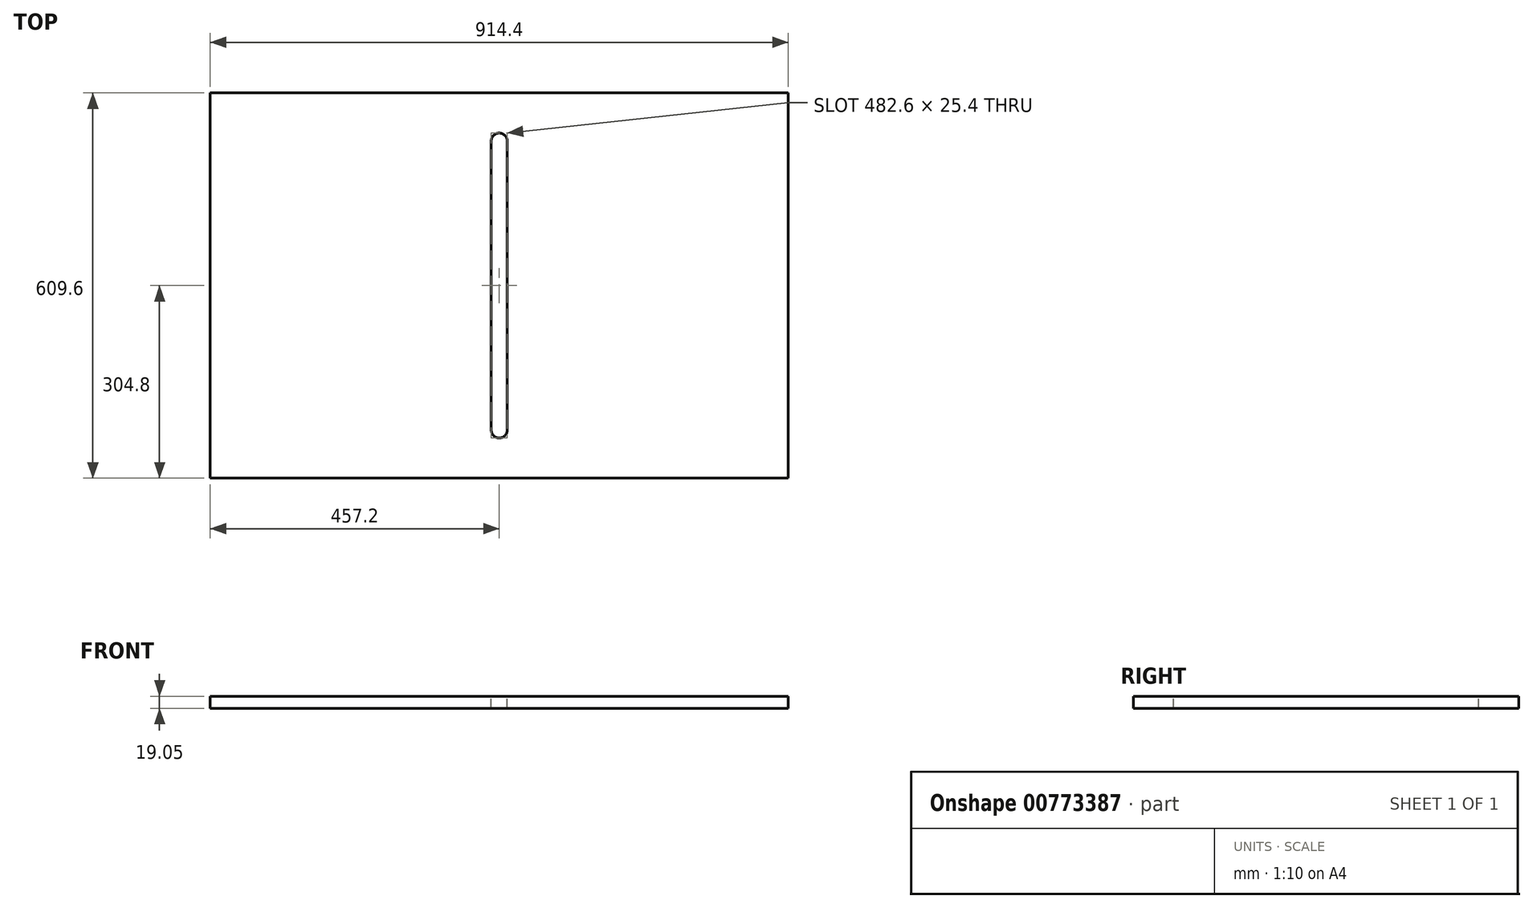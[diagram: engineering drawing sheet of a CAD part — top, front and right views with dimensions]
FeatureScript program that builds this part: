
annotation { "Feature Type Name" : "Feature", "Feature Type Description" : "" }
export const myFeature = defineFeature(function(context is Context, id is Id, definition is map)
    precondition{}
    {
        {
            var Q0;
            Q0=qCreatedBy(makeId("Top.planeOp"),FACE);
            var sketch = newSketch(context, id + "F0", { "sketchPlane" : qUnion([Q0])});
            skLineSegment(sketch, "E0.bottom", {"start": v(457.2, -304.8) * mm, "end": v(-457.2, -304.8) * mm});
            skLineSegment(sketch, "E0.top", {"start": v(457.2, 304.8) * mm, "end": v(-457.2, 304.8) * mm});
            skLineSegment(sketch, "E0.left", {"start": v(457.2, -304.8) * mm, "end": v(457.2, 304.8) * mm});
            skLineSegment(sketch, "E0.right", {"start": v(-457.2, -304.8) * mm, "end": v(-457.2, 304.8) * mm});
            skPoint(sketch, "E0.middle", {"position": v(0, 0) * mm});
            skSolve(sketch);
        }
        {
            var Q0;
            Q0=makeQuery(id+"F0.imprint","IMPRINT",FACE,{"disambiguationData":[TD([[makeQuery(id+"F0.imprint","IMPRINT",EDGE,{"derivedFrom":sQuery(id+"F0.wireOp",EDGE,"E0.bottom")}),-1.0]])]});
            extrude(context, id + "F1", {"entities" : qUnion([Q0]), "depth" : 19.05 * mm, "offsetDistance" : 25.4 * mm});
        }
        {
            var Q0;
            Q0=makeQuery(id+"F1.opExtrude","CAP_FACE",FACE,{"disambiguationData":[OSD([sQuery(id+"F0.wireOp",EDGE,"E0.bottom"),sQuery(id+"F0.wireOp",EDGE,"E0.top"),sQuery(id+"F0.wireOp",EDGE,"E0.left"),sQuery(id+"F0.wireOp",EDGE,"E0.right")])],"isStart":false});
            var sketch = newSketch(context, id + "F2", { "sketchPlane" : qUnion([Q0])});
            skLineSegment(sketch, "E1.bottom", {"start": v(12.7, -228.6) * mm, "end": v(-12.7, -228.6) * mm});
            skLineSegment(sketch, "E1.top", {"start": v(12.7, 228.6) * mm, "end": v(-12.7, 228.6) * mm});
            skLineSegment(sketch, "E1.left", {"start": v(12.7, -228.6) * mm, "end": v(12.7, 228.6) * mm});
            skLineSegment(sketch, "E1.right", {"start": v(-12.7, -228.6) * mm, "end": v(-12.7, 228.6) * mm});
            skPoint(sketch, "E1.middle", {"position": v(0, 0) * mm});
            skLineSegment(sketch, "E2", {"start": v(-12.7, 228.6) * mm, "end": v(0, 228.6) * mm});
            skLineSegment(sketch, "E3", {"start": v(12.7, -228.6) * mm, "end": v(0, -228.6) * mm});
            skCircle(sketch, "E4", {"center": v(0, 228.6) * mm, "radius": 12.7 * mm});
            skCircle(sketch, "E5", {"center": v(0, -228.6) * mm, "radius": 12.7 * mm});
            skSolve(sketch);
        }
        {
            var Q0;
            {var subQ0=sQuery(id+"F2.wireOp",EDGE,"E1.top");Q0=makeQuery(id+"F2.imprint","IMPRINT",FACE,{"disambiguationData":[TD([[makeQuery(id+"F2.imprint","IMPRINT",EDGE,{"derivedFrom":subQ0}),-1.0]])]});}
            var Q1;
            {var subQ0=sQuery(id+"F2.wireOp",EDGE,"E1.top");Q1=makeQuery(id+"F2.imprint","IMPRINT",FACE,{"disambiguationData":[TD([[makeQuery(id+"F2.imprint","IMPRINT",EDGE,{"derivedFrom":subQ0}),1.0]])]});}
            var Q2;
            {var subQ0=sQuery(id+"F2.wireOp",EDGE,"E1.left");Q2=makeQuery(id+"F2.imprint","IMPRINT",FACE,{"disambiguationData":[TD([[makeQuery(id+"F2.imprint","IMPRINT",EDGE,{"derivedFrom":subQ0}),1.0]])]});}
            var Q3;
            {var subQ0=sQuery(id+"F2.wireOp",EDGE,"E1.bottom");Q3=makeQuery(id+"F2.imprint","IMPRINT",FACE,{"disambiguationData":[TD([[makeQuery(id+"F2.imprint","IMPRINT",EDGE,{"derivedFrom":subQ0}),-1.0]])]});}
            var Q4;
            {var subQ0=sQuery(id+"F2.wireOp",EDGE,"E1.bottom");Q4=makeQuery(id+"F2.imprint","IMPRINT",FACE,{"disambiguationData":[TD([[makeQuery(id+"F2.imprint","IMPRINT",EDGE,{"derivedFrom":subQ0}),1.0]])]});}
            extrude(context, id + "F3", {"entities" : qUnion([Q0, Q1, Q2, Q3, Q4]), "operationType" : NewBodyOperationType.REMOVE, "oppositeDirection" : true, "depth" : 25.4 * mm, "offsetDistance" : 25.4 * mm});
        }
    });
